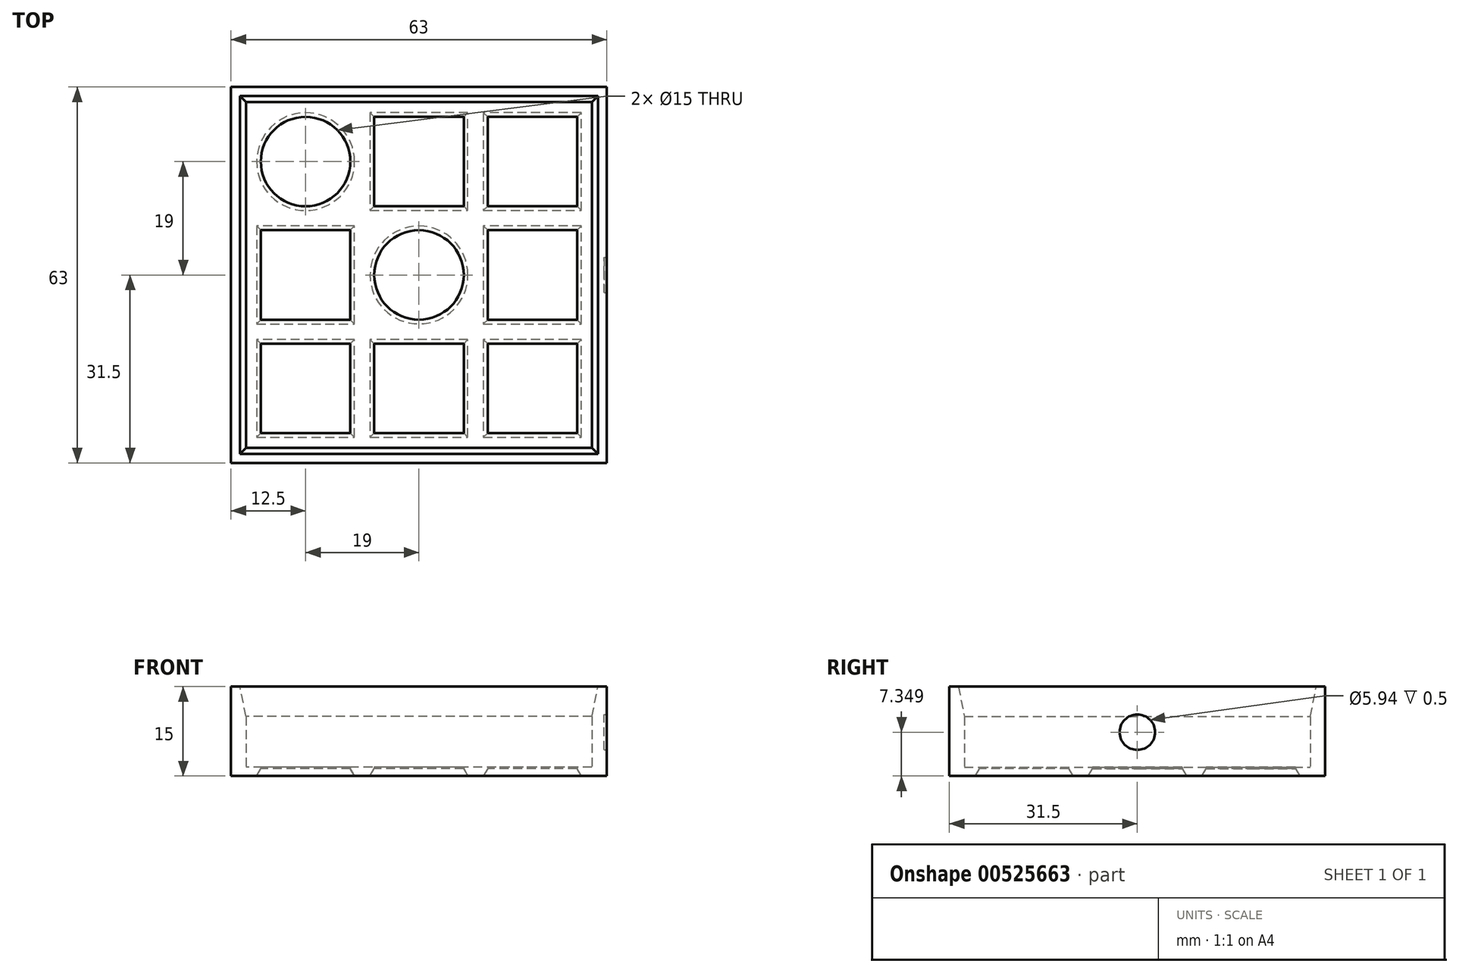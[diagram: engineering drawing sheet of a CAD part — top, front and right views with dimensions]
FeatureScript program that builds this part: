
annotation { "Feature Type Name" : "Feature", "Feature Type Description" : "" }
export const myFeature = defineFeature(function(context is Context, id is Id, definition is map)
    precondition{}
    {
        {
            var Q0;
            Q0=qCreatedBy(makeId("Top.planeOp"),FACE);
            var sketch = newSketch(context, id + "F0", { "sketchPlane" : qUnion([Q0])});
            skLineSegment(sketch, "E0.bottom", {"start": v(29, -29) * mm, "end": v(-29, -29) * mm});
            skLineSegment(sketch, "E0.top", {"start": v(29, 29) * mm, "end": v(-29, 29) * mm});
            skLineSegment(sketch, "E0.left", {"start": v(29, -29) * mm, "end": v(29, 29) * mm});
            skLineSegment(sketch, "E0.right", {"start": v(-29, -29) * mm, "end": v(-29, 29) * mm});
            skPoint(sketch, "E0.middle", {"position": v(0, 0) * mm});
            skLineSegment(sketch, "E1.bottom", {"start": v(19, -19) * mm, "end": v(-19, -19) * mm, "construction": true});
            skLineSegment(sketch, "E1.top", {"start": v(19, 19) * mm, "end": v(-19, 19) * mm, "construction": true});
            skLineSegment(sketch, "E1.left", {"start": v(19, -19) * mm, "end": v(19, 19) * mm, "construction": true});
            skLineSegment(sketch, "E1.right", {"start": v(-19, -19) * mm, "end": v(-19, 19) * mm, "construction": true});
            skCircle(sketch, "E2", {"center": v(-19, 19) * mm, "radius": 7.5 * mm});
            skCircle(sketch, "E3", {"center": v(0, 0) * mm, "radius": 7.5 * mm});
            skLineSegment(sketch, "E4.bottom", {"start": v(7.5, 11.5) * mm, "end": v(-7.5, 11.5) * mm});
            skLineSegment(sketch, "E4.top", {"start": v(7.5, 26.5) * mm, "end": v(-7.5, 26.5) * mm});
            skLineSegment(sketch, "E4.left", {"start": v(7.5, 11.5) * mm, "end": v(7.5, 26.5) * mm});
            skLineSegment(sketch, "E4.right", {"start": v(-7.5, 11.5) * mm, "end": v(-7.5, 26.5) * mm});
            skPoint(sketch, "E4.middle", {"position": v(0, 19) * mm});
            skLineSegment(sketch, "E5.bottom", {"start": v(26.5, 11.5) * mm, "end": v(11.5, 11.5) * mm});
            skLineSegment(sketch, "E5.top", {"start": v(26.5, 26.5) * mm, "end": v(11.5, 26.5) * mm});
            skLineSegment(sketch, "E5.left", {"start": v(26.5, 11.5) * mm, "end": v(26.5, 26.5) * mm});
            skLineSegment(sketch, "E5.right", {"start": v(11.5, 11.5) * mm, "end": v(11.5, 26.5) * mm});
            skPoint(sketch, "E5.middle", {"position": v(19, 19) * mm});
            skLineSegment(sketch, "E6.bottom", {"start": v(26.5, -7.5) * mm, "end": v(11.5, -7.5) * mm});
            skLineSegment(sketch, "E6.top", {"start": v(26.5, 7.5) * mm, "end": v(11.5, 7.5) * mm});
            skLineSegment(sketch, "E6.left", {"start": v(26.5, -7.5) * mm, "end": v(26.5, 7.5) * mm});
            skLineSegment(sketch, "E6.right", {"start": v(11.5, -7.5) * mm, "end": v(11.5, 7.5) * mm});
            skPoint(sketch, "E6.middle", {"position": v(19, 0) * mm});
            skLineSegment(sketch, "E7.bottom", {"start": v(26.5, -26.5) * mm, "end": v(11.5, -26.5) * mm});
            skLineSegment(sketch, "E7.top", {"start": v(26.5, -11.5) * mm, "end": v(11.5, -11.5) * mm});
            skLineSegment(sketch, "E7.left", {"start": v(26.5, -26.5) * mm, "end": v(26.5, -11.5) * mm});
            skLineSegment(sketch, "E7.right", {"start": v(11.5, -26.5) * mm, "end": v(11.5, -11.5) * mm});
            skPoint(sketch, "E7.middle", {"position": v(19, -19) * mm});
            skLineSegment(sketch, "E8.bottom", {"start": v(7.5, -26.5) * mm, "end": v(-7.5, -26.5) * mm});
            skLineSegment(sketch, "E8.top", {"start": v(7.5, -11.5) * mm, "end": v(-7.5, -11.5) * mm});
            skLineSegment(sketch, "E8.left", {"start": v(7.5, -26.5) * mm, "end": v(7.5, -11.5) * mm});
            skLineSegment(sketch, "E8.right", {"start": v(-7.5, -26.5) * mm, "end": v(-7.5, -11.5) * mm});
            skPoint(sketch, "E8.middle", {"position": v(0, -19) * mm});
            skLineSegment(sketch, "E9.bottom", {"start": v(-11.5, -26.5) * mm, "end": v(-26.5, -26.5) * mm});
            skLineSegment(sketch, "E9.top", {"start": v(-11.5, -11.5) * mm, "end": v(-26.5, -11.5) * mm});
            skLineSegment(sketch, "E9.left", {"start": v(-11.5, -26.5) * mm, "end": v(-11.5, -11.5) * mm});
            skLineSegment(sketch, "E9.right", {"start": v(-26.5, -26.5) * mm, "end": v(-26.5, -11.5) * mm});
            skPoint(sketch, "E9.middle", {"position": v(-19, -19) * mm});
            skLineSegment(sketch, "E10.bottom", {"start": v(-11.5, -7.5) * mm, "end": v(-26.5, -7.5) * mm});
            skLineSegment(sketch, "E10.top", {"start": v(-11.5, 7.5) * mm, "end": v(-26.5, 7.5) * mm});
            skLineSegment(sketch, "E10.left", {"start": v(-11.5, -7.5) * mm, "end": v(-11.5, 7.5) * mm});
            skLineSegment(sketch, "E10.right", {"start": v(-26.5, -7.5) * mm, "end": v(-26.5, 7.5) * mm});
            skPoint(sketch, "E10.middle", {"position": v(-19, 0) * mm});
            skSolve(sketch);
        }
        {
            var Q0;
            Q0=makeQuery(id+"F0.imprint","IMPRINT",FACE,{"disambiguationData":[TD([[makeQuery(id+"F0.imprint","IMPRINT",EDGE,{"derivedFrom":sQuery(id+"F0.wireOp",EDGE,"E0.bottom")}),-1.0]])]});
            var Q1;
            Q1=sQuery(id+"F0.wireOp",EDGE,"E1.top");
            var Q2;
            Q2=sQuery(id+"F0.wireOp",EDGE,"E1.right");
            var Q3;
            Q3=sQuery(id+"F0.wireOp",EDGE,"E1.bottom");
            var Q4;
            Q4=sQuery(id+"F0.wireOp",EDGE,"E1.left");
            extrude(context, id + "F1", {"entities" : qUnion([Q0]), "surfaceEntities" : qUnion([Q1, Q2, Q3, Q4]), "depth" : 1.5 * mm, "offsetDistance" : 25 * mm});
        }
        {
            var Q0;
            Q0=qCreatedBy(makeId("Top.planeOp"),FACE);
            var sketch = newSketch(context, id + "F2", { "sketchPlane" : qUnion([Q0])});
            skLineSegment(sketch, "E11.0", {"start": v(31.5, -31.5) * mm, "end": v(31.5, 31.5) * mm});
            skLineSegment(sketch, "E11.1", {"start": v(31.5, -31.5) * mm, "end": v(-31.5, -31.5) * mm});
            skLineSegment(sketch, "E11.2", {"start": v(-31.5, -31.5) * mm, "end": v(-31.5, 31.5) * mm});
            skLineSegment(sketch, "E11.3", {"start": v(31.5, 31.5) * mm, "end": v(-31.5, 31.5) * mm});
            skLineSegment(sketch, "E12.0.0", {"start": v(29, -29) * mm, "end": v(29, 29) * mm});
            skLineSegment(sketch, "E12.0.1", {"start": v(29, 29) * mm, "end": v(-29, 29) * mm});
            skLineSegment(sketch, "E12.0.2", {"start": v(-29, 29) * mm, "end": v(-29, -29) * mm});
            skLineSegment(sketch, "E12.0.3", {"start": v(-29, -29) * mm, "end": v(29, -29) * mm});
            skSolve(sketch);
        }
        {
            var Q0;
            Q0 = qSketchRegion(id + "F2", true);
            extrude(context, id + "F3", {"entities" : qUnion([Q0]), "operationType" : NewBodyOperationType.ADD, "depth" : 15 * mm, "offsetDistance" : 25 * mm});
        }
        {
            var Q0;
            Q0=makeQuery(id+"F1.opExtrude","CAP_EDGE",EDGE,{"disambiguationData":[OSD([sQuery(id+"F0.wireOp",EDGE,"udmZED6G-wypx-mZGj-StYg-nZXOjyNJHCRy")])],"isStart":true});
            var Q1;
            Q1=makeQuery(id+"F1.opExtrude","CAP_EDGE",EDGE,{"disambiguationData":[OSD([sQuery(id+"F0.wireOp",EDGE,"r8ycamZX-F7UL-X00B-81pc-oXJjpk7WTURP")])],"isStart":true});
            var Q2;
            Q2=makeQuery(id+"F1.opExtrude","CAP_EDGE",EDGE,{"disambiguationData":[OSD([sQuery(id+"F0.wireOp",EDGE,"E2")])],"isStart":true});
            var Q3;
            Q3=makeQuery(id+"F1.opExtrude","CAP_EDGE",EDGE,{"disambiguationData":[OSD([sQuery(id+"F0.wireOp",EDGE,"LAMa4kOX-jxZ0-Aw7w-x1jK-5QTgVkBVv3I3")])],"isStart":true});
            var Q4;
            Q4=makeQuery(id+"F1.opExtrude","CAP_EDGE",EDGE,{"disambiguationData":[OSD([sQuery(id+"F0.wireOp",EDGE,"PVzw60BU-HPo9-mHgr-RNro-DBZP9GjZv3gG")])],"isStart":true});
            var Q5;
            Q5=makeQuery(id+"F1.opExtrude","CAP_EDGE",EDGE,{"disambiguationData":[OSD([sQuery(id+"F0.wireOp",EDGE,"Bo5tVZRF-vPpy-uiYF-fDm4-n6rwyC5MyM1a")])],"isStart":true});
            var Q6;
            Q6=makeQuery(id+"F1.opExtrude","CAP_EDGE",EDGE,{"disambiguationData":[OSD([sQuery(id+"F0.wireOp",EDGE,"NcBLgyUn-ObsX-BnBF-G8BW-nVKHcu7z8yDE")])],"isStart":true});
            var Q7;
            Q7=makeQuery(id+"F1.opExtrude","CAP_EDGE",EDGE,{"disambiguationData":[OSD([sQuery(id+"F0.wireOp",EDGE,"r1j9TIeG-6yAQ-5Z6Z-jpGh-hXjQCbXWvg5a")])],"isStart":true});
            var Q8;
            Q8=makeQuery(id+"F1.opExtrude","CAP_EDGE",EDGE,{"disambiguationData":[OSD([sQuery(id+"F0.wireOp",EDGE,"E3")])],"isStart":true});
            var Q9;
            Q9=makeQuery(id+"F1.opExtrude","CAP_EDGE",EDGE,{"disambiguationData":[OSD([sQuery(id+"F0.wireOp",EDGE,"E10.left")])],"isStart":true});
            var Q10;
            Q10=makeQuery(id+"F1.opExtrude","CAP_EDGE",EDGE,{"disambiguationData":[OSD([sQuery(id+"F0.wireOp",EDGE,"E10.top")])],"isStart":true});
            var Q11;
            Q11=makeQuery(id+"F1.opExtrude","CAP_EDGE",EDGE,{"disambiguationData":[OSD([sQuery(id+"F0.wireOp",EDGE,"E10.right")])],"isStart":true});
            var Q12;
            Q12=makeQuery(id+"F1.opExtrude","CAP_EDGE",EDGE,{"disambiguationData":[OSD([sQuery(id+"F0.wireOp",EDGE,"E10.bottom")])],"isStart":true});
            var Q13;
            Q13=makeQuery(id+"F1.opExtrude","CAP_EDGE",EDGE,{"disambiguationData":[OSD([sQuery(id+"F0.wireOp",EDGE,"E9.top")])],"isStart":true});
            var Q14;
            Q14=makeQuery(id+"F1.opExtrude","CAP_EDGE",EDGE,{"disambiguationData":[OSD([sQuery(id+"F0.wireOp",EDGE,"E9.left")])],"isStart":true});
            var Q15;
            Q15=makeQuery(id+"F1.opExtrude","CAP_EDGE",EDGE,{"disambiguationData":[OSD([sQuery(id+"F0.wireOp",EDGE,"E9.right")])],"isStart":true});
            var Q16;
            Q16=makeQuery(id+"F1.opExtrude","CAP_EDGE",EDGE,{"disambiguationData":[OSD([sQuery(id+"F0.wireOp",EDGE,"E9.bottom")])],"isStart":true});
            var Q17;
            Q17=makeQuery(id+"F1.opExtrude","CAP_EDGE",EDGE,{"disambiguationData":[OSD([sQuery(id+"F0.wireOp",EDGE,"E8.bottom")])],"isStart":true});
            var Q18;
            Q18=makeQuery(id+"F1.opExtrude","CAP_EDGE",EDGE,{"disambiguationData":[OSD([sQuery(id+"F0.wireOp",EDGE,"E8.right")])],"isStart":true});
            var Q19;
            Q19=makeQuery(id+"F1.opExtrude","CAP_EDGE",EDGE,{"disambiguationData":[OSD([sQuery(id+"F0.wireOp",EDGE,"E8.top")])],"isStart":true});
            var Q20;
            Q20=makeQuery(id+"F1.opExtrude","CAP_EDGE",EDGE,{"disambiguationData":[OSD([sQuery(id+"F0.wireOp",EDGE,"E8.left")])],"isStart":true});
            var Q21;
            Q21=makeQuery(id+"F1.opExtrude","CAP_EDGE",EDGE,{"disambiguationData":[OSD([sQuery(id+"F0.wireOp",EDGE,"E7.right")])],"isStart":true});
            var Q22;
            Q22=makeQuery(id+"F1.opExtrude","CAP_EDGE",EDGE,{"disambiguationData":[OSD([sQuery(id+"F0.wireOp",EDGE,"E7.top")])],"isStart":true});
            var Q23;
            Q23=makeQuery(id+"F1.opExtrude","CAP_EDGE",EDGE,{"disambiguationData":[OSD([sQuery(id+"F0.wireOp",EDGE,"E7.left")])],"isStart":true});
            var Q24;
            Q24=makeQuery(id+"F1.opExtrude","CAP_EDGE",EDGE,{"disambiguationData":[OSD([sQuery(id+"F0.wireOp",EDGE,"E7.bottom")])],"isStart":true});
            var Q25;
            Q25=makeQuery(id+"F1.opExtrude","CAP_EDGE",EDGE,{"disambiguationData":[OSD([sQuery(id+"F0.wireOp",EDGE,"E6.bottom")])],"isStart":true});
            var Q26;
            Q26=makeQuery(id+"F1.opExtrude","CAP_EDGE",EDGE,{"disambiguationData":[OSD([sQuery(id+"F0.wireOp",EDGE,"E6.right")])],"isStart":true});
            var Q27;
            Q27=makeQuery(id+"F1.opExtrude","CAP_EDGE",EDGE,{"disambiguationData":[OSD([sQuery(id+"F0.wireOp",EDGE,"E6.top")])],"isStart":true});
            var Q28;
            Q28=makeQuery(id+"F1.opExtrude","CAP_EDGE",EDGE,{"disambiguationData":[OSD([sQuery(id+"F0.wireOp",EDGE,"E6.left")])],"isStart":true});
            var Q29;
            Q29=makeQuery(id+"F1.opExtrude","CAP_EDGE",EDGE,{"disambiguationData":[OSD([sQuery(id+"F0.wireOp",EDGE,"E5.bottom")])],"isStart":true});
            var Q30;
            Q30=makeQuery(id+"F1.opExtrude","CAP_EDGE",EDGE,{"disambiguationData":[OSD([sQuery(id+"F0.wireOp",EDGE,"E5.right")])],"isStart":true});
            var Q31;
            Q31=makeQuery(id+"F1.opExtrude","CAP_EDGE",EDGE,{"disambiguationData":[OSD([sQuery(id+"F0.wireOp",EDGE,"E5.top")])],"isStart":true});
            var Q32;
            Q32=makeQuery(id+"F1.opExtrude","CAP_EDGE",EDGE,{"disambiguationData":[OSD([sQuery(id+"F0.wireOp",EDGE,"E5.left")])],"isStart":true});
            var Q33;
            Q33=makeQuery(id+"F1.opExtrude","CAP_EDGE",EDGE,{"disambiguationData":[OSD([sQuery(id+"F0.wireOp",EDGE,"E4.left")])],"isStart":true});
            var Q34;
            Q34=makeQuery(id+"F1.opExtrude","CAP_EDGE",EDGE,{"disambiguationData":[OSD([sQuery(id+"F0.wireOp",EDGE,"E4.bottom")])],"isStart":true});
            var Q35;
            Q35=makeQuery(id+"F1.opExtrude","CAP_EDGE",EDGE,{"disambiguationData":[OSD([sQuery(id+"F0.wireOp",EDGE,"E4.right")])],"isStart":true});
            var Q36;
            Q36=makeQuery(id+"F1.opExtrude","CAP_EDGE",EDGE,{"disambiguationData":[OSD([sQuery(id+"F0.wireOp",EDGE,"E4.top")])],"isStart":true});
            chamfer(context, id + "F4", {"entities" : qUnion([Q0, Q1, Q2, Q3, Q4, Q5, Q6, Q7, Q8, Q9, Q10, Q11, Q12, Q13, Q14, Q15, Q16, Q17, Q18, Q19, Q20, Q21, Q22, Q23, Q24, Q25, Q26, Q27, Q28, Q29, Q30, Q31, Q32, Q33, Q34, Q35, Q36]), "chamferType" : ChamferType.OFFSET_ANGLE, "width" : 0.7 * mm, "oppositeDirection" : false, "angle" : 60 * degree, "tangentPropagation" : true});
        }
        {
            var Q0;
            Q0=makeQuery(id+"F3.opExtrude","CAP_EDGE",EDGE,{"disambiguationData":[OSD([sQuery(id+"F2.wireOp",EDGE,"E12.0.2")])],"isStart":false});
            var Q1;
            Q1=makeQuery(id+"F3.opExtrude","CAP_EDGE",EDGE,{"disambiguationData":[OSD([sQuery(id+"F2.wireOp",EDGE,"E12.0.1")])],"isStart":false});
            var Q2;
            Q2=makeQuery(id+"F3.opExtrude","CAP_EDGE",EDGE,{"disambiguationData":[OSD([sQuery(id+"F2.wireOp",EDGE,"E12.0.0")])],"isStart":false});
            var Q3;
            Q3=makeQuery(id+"F3.opExtrude","CAP_EDGE",EDGE,{"disambiguationData":[OSD([sQuery(id+"F2.wireOp",EDGE,"E12.0.3")])],"isStart":false});
            chamfer(context, id + "F5", {"entities" : qUnion([Q0, Q1, Q2, Q3]), "chamferType" : ChamferType.TWO_OFFSETS, "width1" : 1 * mm, "oppositeDirection" : true, "width2" : 5 * mm, "tangentPropagation" : true});
        }
        {
            var Q0;
            Q0=makeQuery(id+"F3.opExtrude","SWEPT_FACE",FACE,{"disambiguationData":[OSD([sQuery(id+"F2.wireOp",EDGE,"E11.0")])]});
            var sketch = newSketch(context, id + "F6", { "sketchPlane" : qUnion([Q0])});
            skCircle(sketch, "E13", {"center": v(0, 7.35) * mm, "radius": 2.97 * mm});
            skSolve(sketch);
        }
        {
            var Q0;
            Q0=makeQuery(id+"F6.imprint","IMPRINT",FACE,{"disambiguationData":[TD([[makeQuery(id+"F6.imprint","IMPRINT",EDGE,{"derivedFrom":sQuery(id+"F6.wireOp",EDGE,"E13")}),1.0]])]});
            extrude(context, id + "F7", {"entities" : qUnion([Q0]), "operationType" : NewBodyOperationType.REMOVE, "oppositeDirection" : true, "depth" : 0.5 * mm, "offsetDistance" : 25 * mm});
        }
    });
